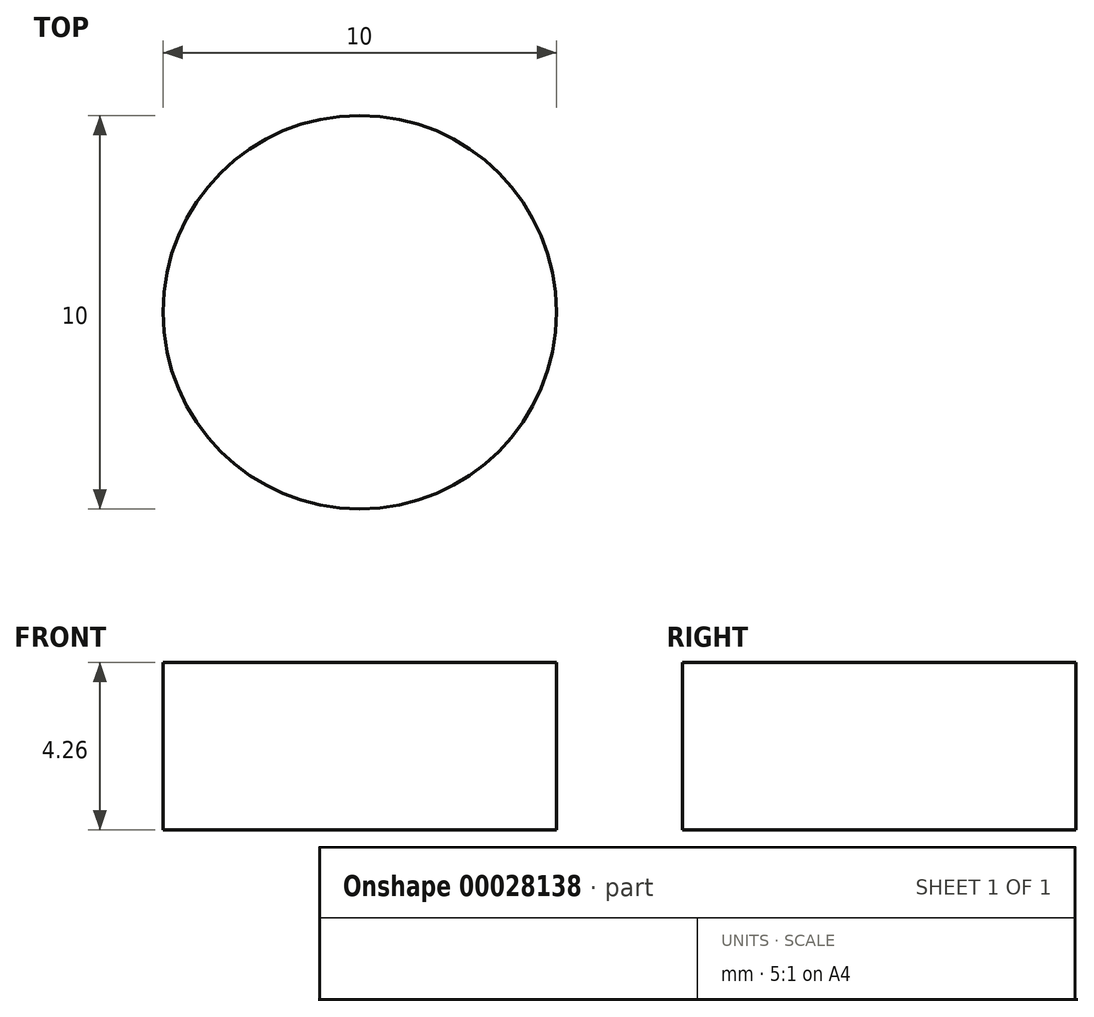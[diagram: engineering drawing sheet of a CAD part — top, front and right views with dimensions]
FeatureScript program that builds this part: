
annotation { "Feature Type Name" : "Feature", "Feature Type Description" : "" }
export const myFeature = defineFeature(function(context is Context, id is Id, definition is map)
    precondition{}
    {
        {
            var Q0;
            Q0=qCreatedBy(makeId("Front.planeOp"),FACE);
            var sketch = newSketch(context, id + "F0", { "sketchPlane" : qUnion([Q0])});
            skLineSegment(sketch, "E0.bottom", {"start": v(0, 0) * mm, "end": v(10, 0) * mm});
            skLineSegment(sketch, "E0.top", {"start": v(0, 4.26) * mm, "end": v(10, 4.26) * mm});
            skLineSegment(sketch, "E0.left", {"start": v(0, 0) * mm, "end": v(0, 4.26) * mm});
            skLineSegment(sketch, "E0.right", {"start": v(10, 0) * mm, "end": v(10, 4.26) * mm});
            skCircle(sketch, "E1", {"center": v(10, 0.5) * mm, "radius": 0.5 * mm});
            skCircle(sketch, "E2", {"center": v(10, 1.5) * mm, "radius": 0.5 * mm});
            skLineSegment(sketch, "E3.bottom", {"start": v(0, 0) * mm, "end": v(5, 0) * mm});
            skLineSegment(sketch, "E3.top", {"start": v(0, 4.26) * mm, "end": v(5, 4.26) * mm});
            skLineSegment(sketch, "E3.right", {"start": v(5, 0) * mm, "end": v(5, 4.26) * mm});
            skSolve(sketch);
        }
        {
            var Q0;
            {var subQ4=sQuery(id+"F0.wireOp",EDGE,"E0.bottom");Q0=makeQuery(id+"F0.imprint","IMPRINT",FACE,{"disambiguationData":[TD([[makeQuery(id+"F0.imprint","IMPRINT",EDGE,{"derivedFrom":subQ4}),1.0]])]});}
            var Q1;
            Q1=sQuery(id+"F0.wireOp",EDGE,"E0.left");
            revolve(context, id + "F1", {"entities" : qUnion([Q0]), "axis" : qUnion([Q1]), "revolveType" : RevolveType.FULL});
        }
        {
            var Q0;
            Q0=makeQuery(id+"F1.opRevolve","SWEPT_FACE",FACE,{"disambiguationData":[OSD([sQuery(id+"F0.wireOp",EDGE,"E0.top")])]});
            var sketch = newSketch(context, id + "F2", { "sketchPlane" : qUnion([Q0])});
            skCircle(sketch, "E4", {"center": v(0, 10) * mm, "radius": 2 * mm});
            skCircle(sketch, "E5", {"center": v(0, -10) * mm, "radius": 1 * mm});
            skSolve(sketch);
        }
        {
            var Q0;
            {var subQ0=makeQuery(id+"F1.opRevolve","SWEPT_EDGE",EDGE,{"disambiguationData":[OSD([sQuery(id+"F0.wireOp",EDGE,"E0.top"),sQuery(id+"F0.wireOp",EDGE,"E0.right")])]});var subQ1=sQuery(id+"F2.wireOp",EDGE,"E4");var subQ3=makeQuery(id+"F2.imprint","INTERSECT",VERTEX,{"disambiguationData":[OD(0.0)],"derivedFrom":[subQ0,subQ1]});Q0=makeQuery(id+"F2.imprint","IMPRINT",FACE,{"disambiguationData":[TD([[makeQuery(id+"F2.imprint","IMPRINT",EDGE,{"disambiguationData":[TD([[subQ3,-1.0]])],"derivedFrom":subQ1}),1.0]])]});}
            extrude(context, id + "F3", {"entities" : qUnion([Q0]), "operationType" : NewBodyOperationType.REMOVE, "oppositeDirection" : true, "depth" : 3.28 * mm});
        }
        {
            var Q0;
            {var subQ0=makeQuery(id+"F1.opRevolve","SWEPT_EDGE",EDGE,{"disambiguationData":[OSD([sQuery(id+"F0.wireOp",EDGE,"E0.top"),sQuery(id+"F0.wireOp",EDGE,"E0.right")])]});var subQ1=sQuery(id+"F2.wireOp",EDGE,"E5");var subQ3=makeQuery(id+"F2.imprint","INTERSECT",VERTEX,{"disambiguationData":[OD(0.0)],"derivedFrom":[subQ0,subQ1]});Q0=makeQuery(id+"F2.imprint","IMPRINT",FACE,{"disambiguationData":[TD([[makeQuery(id+"F2.imprint","IMPRINT",EDGE,{"disambiguationData":[TD([[subQ3,1.0]])],"derivedFrom":subQ1}),1.0]])]});}
            extrude(context, id + "F4", {"entities" : qUnion([Q0]), "operationType" : NewBodyOperationType.REMOVE, "oppositeDirection" : true, "depth" : 4.12 * mm});
        }
    });
